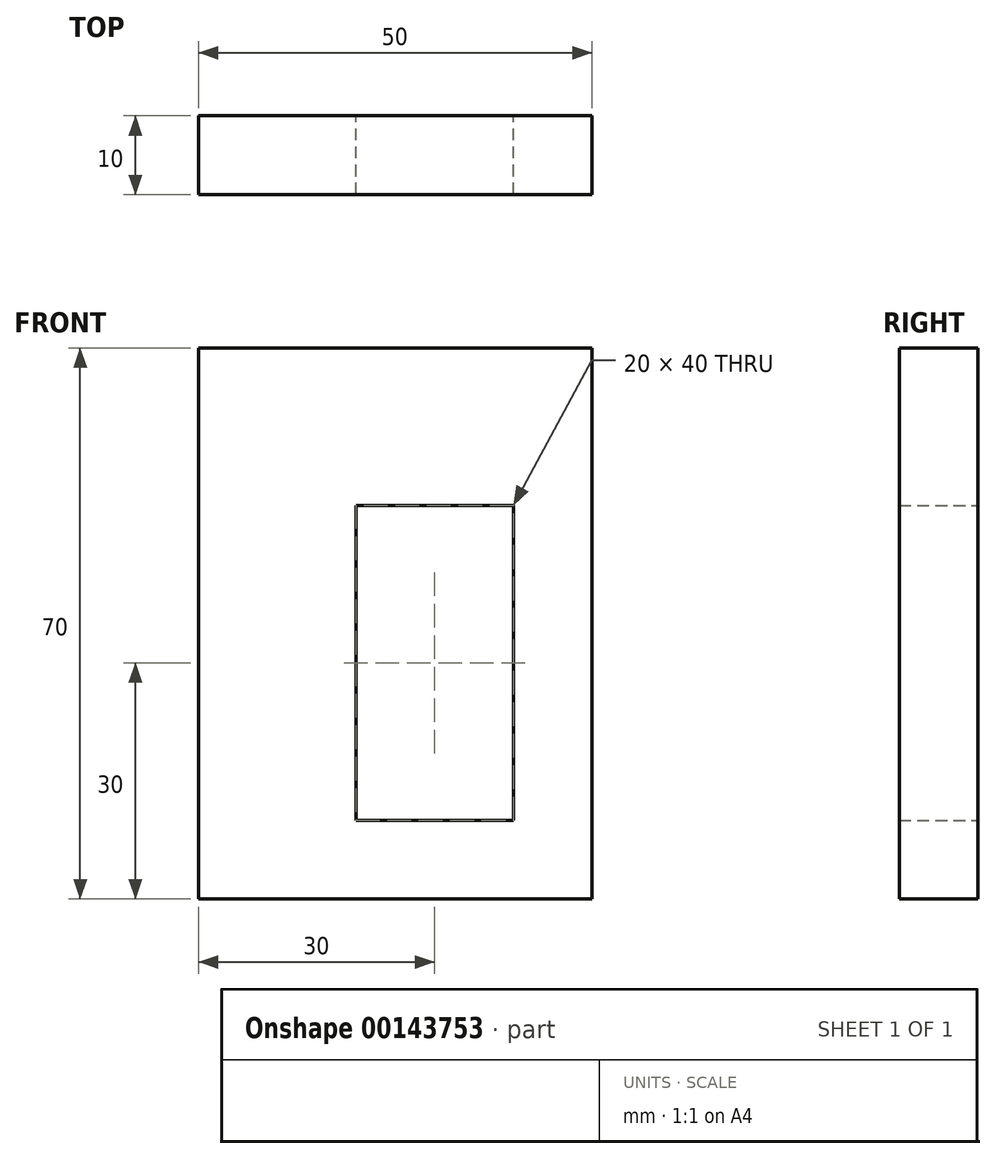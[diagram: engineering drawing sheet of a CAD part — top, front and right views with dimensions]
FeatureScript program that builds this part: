
annotation { "Feature Type Name" : "Feature", "Feature Type Description" : "" }
export const myFeature = defineFeature(function(context is Context, id is Id, definition is map)
    precondition{}
    {
        {
            var Q0;
            Q0=qCreatedBy(makeId("Front.planeOp"),FACE);
            var sketch = newSketch(context, id + "F0", { "sketchPlane" : qUnion([Q0])});
            skLineSegment(sketch, "E0", {"start": v(0, 70) * mm, "end": v(0, 0) * mm});
            skLineSegment(sketch, "E1", {"start": v(0, 0) * mm, "end": v(50, 0) * mm});
            skLineSegment(sketch, "E2", {"start": v(50, 0) * mm, "end": v(50, 70) * mm});
            skLineSegment(sketch, "E3", {"start": v(50, 70) * mm, "end": v(0, 70) * mm});
            skLineSegment(sketch, "E4", {"start": v(20, 50) * mm, "end": v(20, 10) * mm});
            skLineSegment(sketch, "E5", {"start": v(20, 10) * mm, "end": v(40, 10) * mm});
            skLineSegment(sketch, "E6", {"start": v(40, 10) * mm, "end": v(40, 50) * mm});
            skLineSegment(sketch, "E7", {"start": v(40, 50) * mm, "end": v(20, 50) * mm});
            skSolve(sketch);
        }
        {
            var Q0;
            Q0=qSketchRegion(id+"F0",true);
            extrude(context, id + "F1", {"entities" : qUnion([Q0]), "depth" : 10 * mm});
        }
    });
